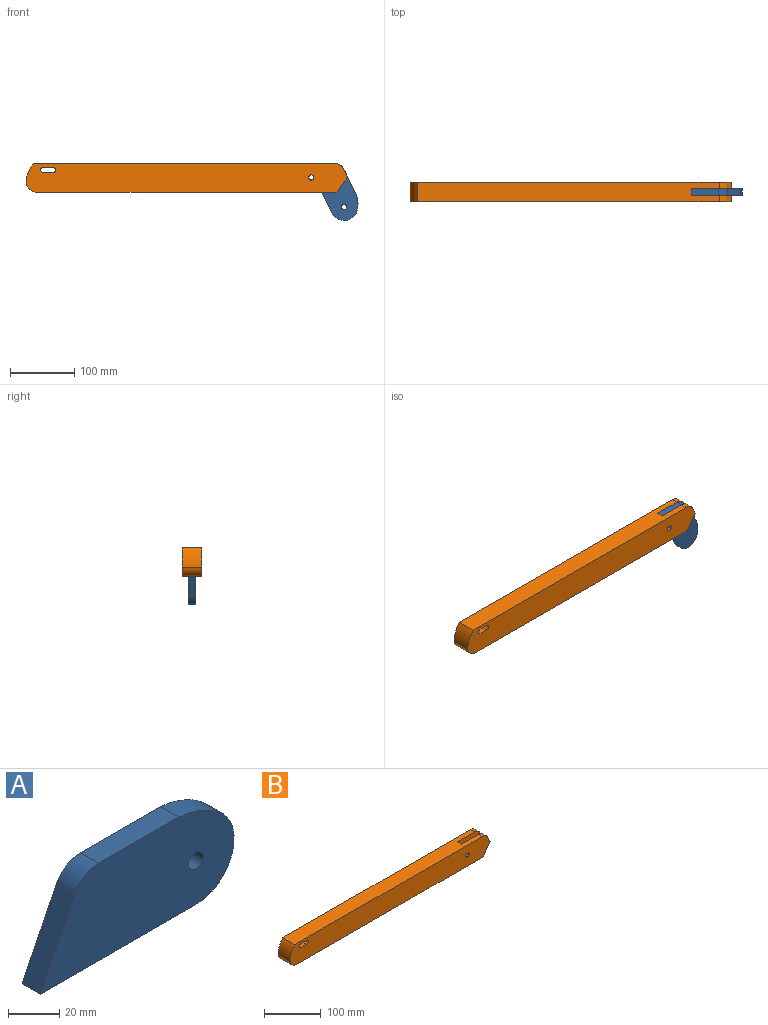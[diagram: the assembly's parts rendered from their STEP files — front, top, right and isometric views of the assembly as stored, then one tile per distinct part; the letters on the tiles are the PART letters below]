
ASSEMBLY  parts=2 mates=1
PART A: 9 faces, bbox 106.8x10x46.4 mm
  f0: cylinder r=20.99mm len=37.33mm, axis (0,1,0), area 525.7mm2, adj f1,f5,f7,f8
  f1: cylinder r=41.77mm len=22.7mm, axis (0,1,0), area 248.1mm2, adj f0,f2,f7,f8
  f2: plane 44.08x10mm, normal (0,0,1), area 440.8mm2, adj f1,f3,f7,f8
  f3: cylinder r=14.73mm len=13.19mm, axis (0,1,0), area 163.3mm2, adj f2,f4,f7,f8
  f4: plane 38.24x19.04mm, normal (-0.9,0,0.45), area 427.1mm2, adj f3,f5,f7,f8
  f5: plane 84.98x10mm, normal (0,0,-1), area 849.7mm2, adj f0,f4,f7,f8
  f6: cylinder r=4mm len=10mm, axis (0,1,0), area 251.3mm2, adj f7,f8
  f7: plane 106.83x46.42mm, normal (0,-1,0), area 4079.3mm2, adj f0,f1,f2,f3,f4,f5,f6
  f8: plane 106.83x46.42mm, normal (0,1,0), area 4079.3mm2, adj f0,f1,f2,f3,f4,f5,f6
PART B: 20 faces, bbox 499.2x30x45.4 mm
  f0: plane 468x30mm, normal (0,0,1), area 13612.5mm2, adj f4,f8,f12,f15,f16,f17,f18,f19
  f1: plane 464.09x30mm, normal (0,0,-1), area 13697.7mm2, adj f2,f9,f10,f15,f16,f17,f18,f19
  f2: plane 24.45x16.92mm, normal (0.82,0,-0.57), area 297.3mm2, adj f1,f3,f15,f18
  f3: plane 11.49x10mm, normal (0.9,0,0.44), area 128.2mm2, adj f2,f4,f15,f18
  f4: cylinder r=14.83mm len=13.65mm, axis (0,1,0), area 173.6mm2, adj f0,f3,f15,f18
  f5: cylinder r=4mm len=30mm, axis (0,1,0), area 377mm2, adj f6,f14,f15,f16
  f6: plane 30x15mm, normal (0,0,-1), area 450mm2, adj f5,f7,f15,f16
  f7: cylinder r=4mm len=30mm, axis (0,1,0), area 377mm2, adj f6,f14,f15,f16
  f8: cylinder r=46.01mm len=30.73mm, axis (0,1,0), area 1011.2mm2, adj f0,f9,f15,f16
  f9: cylinder r=17.66mm len=30mm, axis (0,1,0), area 757.6mm2, adj f1,f8,f15,f16
  f10: plane 24.45x16.92mm, normal (0.82,0,-0.57), area 297.3mm2, adj f1,f11,f16,f19
  f11: plane 11.49x10mm, normal (0.9,0,0.44), area 128.2mm2, adj f10,f12,f16,f19
  f12: cylinder r=14.83mm len=13.65mm, axis (0,1,0), area 173.6mm2, adj f0,f11,f16,f19
  f13: cylinder r=4mm len=30mm, axis (0,1,0), area 754mm2, adj f15,f16
  f14: plane 30x15mm, normal (0,0,1), area 450mm2, adj f5,f7,f15,f16
  f15: plane 499.24x45.39mm, normal (0,-1,0), area 21743.1mm2, adj f0,f1,f2,f3,f4,f5,f6,f7
  f16: plane 499.24x45.39mm, normal (0,1,0), area 21743.1mm2, adj f0,f1,f5,f6,f7,f8,f9,f10
  f17: plane 45.02x22.66mm, normal (0.89,0,0.45), area 504mm2, adj f0,f1,f18,f19
  f18: plane 62.08x45.04mm, normal (0,1,0), area 1958.8mm2, adj f0,f1,f2,f3,f4,f17
  f19: plane 62.08x45.04mm, normal (0,-1,0), area 1958.8mm2, adj f0,f1,f10,f11,f12,f17
PLACE A rot(axis=(0,1,0),63.6deg) t=(219.19,-9.26,-28.15)mm
PLACE B t=(-6.68,0.74,-20.27)mm
MATE fastened A.f4 <-> B.f0  axis (0,0,1) through (181.18,-14.26,1.24)mm
